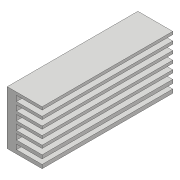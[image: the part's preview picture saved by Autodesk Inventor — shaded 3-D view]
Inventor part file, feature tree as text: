
AUTODESK INVENTOR PART (.ipt)
format: ipt  version: 2018 (Build 220112000, 112)  size: 151,040 bytes
history: native  units: mm
features: extrude x5, sketch x5, projected_geometry x2, mirror x1, pattern_linear x1
ambient origin geometry x8: Origin, YZ Plane, XZ Plane, XY Plane, X Axis, Y Axis, Z Axis, Center Point
bodies: Solid1 (feature_tree)
feature tree (14):
  extrude  "Extrusion1"  Depth=40.0mm
  extrude  "Extrusion2"  Depth=1.7mm
  mirror  "Mirror1"
  extrude  "Extrusion3"  Depth=2.2mm
  pattern_linear  "Rectangular Pattern1"  Spacing1=2.52mm  [1 undecoded]
  extrude  "Extrusion4"  Depth=3.82mm TaperAngle=0.0deg
  extrude  "Extrusion5"  Depth=3.82mm
  sketch  "Sketch1"  dims[d0=20.0mm d1=40.0mm]
  sketch  "Sketch2"  dims[d2=60.0mm d3=0.0mm d4=1.7mm]
  projected_geometry  "Projected Loop1"
  sketch  "Sketch3"  dims[d5=4.2mm d6=2.2mm]
  projected_geometry  "Projected Loop2"
  sketch  "Sketch4"  dims[d7=85.0mm d8=0.0mm]
  sketch  "Sketch5"  dims[d9=1.3mm d10=2.52mm d11=85.0mm d12=0.0mm d13=80.0mm d15=3.82mm d16=10.0mm d17=0.0mm d18=4.0mm d19=0.0mm]
note: 1 required parameter value undecoded (feature->parameter linkage not recoverable at this tier; creation-order binding heuristic only, values carry confidence <= 0.55)
